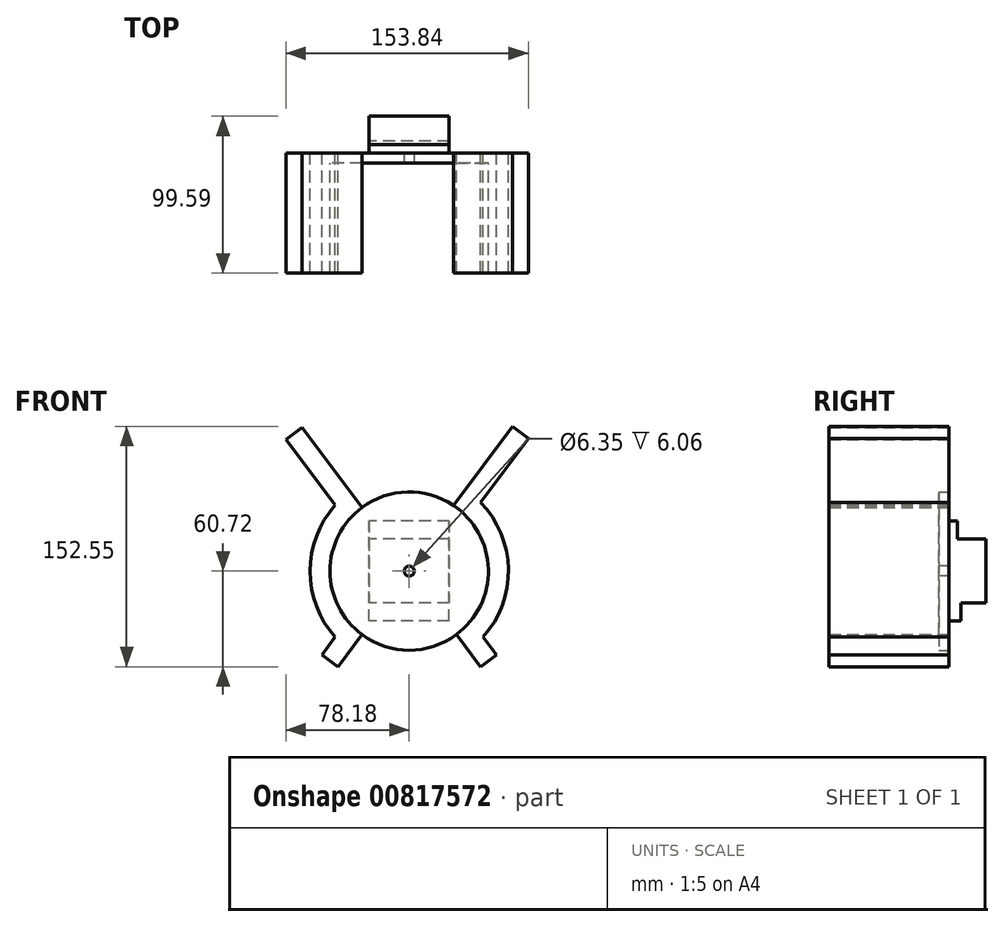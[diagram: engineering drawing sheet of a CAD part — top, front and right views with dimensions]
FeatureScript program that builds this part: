
annotation { "Feature Type Name" : "Feature", "Feature Type Description" : "" }
export const myFeature = defineFeature(function(context is Context, id is Id, definition is map)
    precondition{}
    {
        {
            var Q0;
            Q0=qCreatedBy(makeId("Front.planeOp"),FACE);
            var sketch = newSketch(context, id + "F0", { "sketchPlane" : qUnion([Q0])});
            skCircle(sketch, "E0", {"center": v(0, 0) * mm, "radius": 50.3 * mm});
            skLineSegment(sketch, "E1", {"start": v(-29.97, 40.39) * mm, "end": v(-68, 91.23) * mm});
            skLineSegment(sketch, "E2", {"start": v(-29.97, -40.39) * mm, "end": v(-45.19, -60.72) * mm});
            skLineSegment(sketch, "E3", {"start": v(29.97, -40.39) * mm, "end": v(45.19, -60.72) * mm});
            skLineSegment(sketch, "E4", {"start": v(65.5, 91.83) * mm, "end": v(75.66, 84.22) * mm});
            skLineSegment(sketch, "E5", {"start": v(75.66, 84.22) * mm, "end": v(37.62, 33.37) * mm});
            skLineSegment(sketch, "E6", {"start": v(-68, 91.23) * mm, "end": v(-78.18, 83.63) * mm});
            skLineSegment(sketch, "E7", {"start": v(-78.18, 83.63) * mm, "end": v(-39.2, 31.51) * mm});
            skLineSegment(sketch, "E8", {"start": v(-45.19, -60.72) * mm, "end": v(-55.36, -53.12) * mm});
            skLineSegment(sketch, "E9", {"start": v(-55.36, -53.12) * mm, "end": v(-39.2, -31.51) * mm});
            skLineSegment(sketch, "E10", {"start": v(45.19, -60.72) * mm, "end": v(55.36, -53.12) * mm});
            skLineSegment(sketch, "E11", {"start": v(55.36, -53.12) * mm, "end": v(39.2, -31.51) * mm});
            skLineSegment(sketch, "E12", {"start": v(65.5, 91.83) * mm, "end": v(28.03, 41.75) * mm});
            skCircle(sketch, "E13.0", {"center": v(0, 0) * mm, "radius": 63 * mm});
            skSolve(sketch);
        }
        {
            var Q0;
            {var subQ0=sQuery(id+"F0.wireOp",EDGE,"E1");Q0=makeQuery(id+"F0.imprint","IMPRINT",FACE,{"disambiguationData":[TD([[makeQuery(id+"F0.imprint","IMPRINT",EDGE,{"derivedFrom":subQ0}),1.0]])]});}
            var Q1;
            {var subQ4=sQuery(id+"F0.wireOp",EDGE,"E4");Q1=makeQuery(id+"F0.imprint","IMPRINT",FACE,{"disambiguationData":[TD([[makeQuery(id+"F0.imprint","IMPRINT",EDGE,{"derivedFrom":subQ4}),-1.0]])]});}
            var Q2;
            {var subQ0=sQuery(id+"F0.wireOp",EDGE,"E3");Q2=makeQuery(id+"F0.imprint","IMPRINT",FACE,{"disambiguationData":[TD([[makeQuery(id+"F0.imprint","IMPRINT",EDGE,{"derivedFrom":subQ0}),1.0]])]});}
            var Q3;
            {var subQ0=sQuery(id+"F0.wireOp",EDGE,"E2");Q3=makeQuery(id+"F0.imprint","IMPRINT",FACE,{"disambiguationData":[TD([[makeQuery(id+"F0.imprint","IMPRINT",EDGE,{"derivedFrom":subQ0}),-1.0]])]});}
            var Q4;
            {var subQ0=sQuery(id+"F0.wireOp",EDGE,"E5");var subQ1=sQuery(id+"F0.wireOp",EDGE,"E0");var subQ2=makeQuery(id+"F0.imprint","INTERSECT",VERTEX,{"derivedFrom":[subQ1,subQ0]});Q4=makeQuery(id+"F0.imprint","IMPRINT",FACE,{"disambiguationData":[TD([[makeQuery(id+"F0.imprint","IMPRINT",EDGE,{"disambiguationData":[TD([[subQ2,-1.0]])],"derivedFrom":subQ1}),-1.0]])]});}
            var Q5;
            {var subQ0=sQuery(id+"F0.wireOp",EDGE,"E7");var subQ1=sQuery(id+"F0.wireOp",EDGE,"E0");var subQ2=makeQuery(id+"F0.imprint","INTERSECT",VERTEX,{"derivedFrom":[subQ1,subQ0]});Q5=makeQuery(id+"F0.imprint","IMPRINT",FACE,{"disambiguationData":[TD([[makeQuery(id+"F0.imprint","IMPRINT",EDGE,{"disambiguationData":[TD([[subQ2,-1.0]])],"derivedFrom":subQ1}),-1.0]])]});}
            var Q6;
            {var subQ0=sQuery(id+"F0.wireOp",EDGE,"E5");var subQ1=sQuery(id+"F0.wireOp",EDGE,"E0");var subQ2=makeQuery(id+"F0.imprint","INTERSECT",VERTEX,{"derivedFrom":[subQ1,subQ0]});Q6=makeQuery(id+"F0.imprint","IMPRINT",FACE,{"disambiguationData":[TD([[makeQuery(id+"F0.imprint","IMPRINT",EDGE,{"disambiguationData":[TD([[subQ2,1.0]])],"derivedFrom":subQ1}),-1.0]])]});}
            var Q7;
            {var subQ0=sQuery(id+"F0.wireOp",EDGE,"E0");var subQ5=makeQuery(id+"F0.imprint","INTERSECT",VERTEX,{"derivedFrom":[subQ0,sQuery(id+"F0.wireOp",EDGE,"E5")]});Q7=makeQuery(id+"F0.imprint","IMPRINT",FACE,{"disambiguationData":[TD([[makeQuery(id+"F0.imprint","IMPRINT",EDGE,{"disambiguationData":[TD([[subQ5,-1.0]])],"derivedFrom":subQ0}),1.0]])]});}
            extrude(context, id + "F1", {"entities" : qUnion([Q0, Q1, Q2, Q3, Q4, Q5, Q6, Q7]), "endBound" : BoundingType.SYMMETRIC, "depth" : 76.2 * mm, "offsetDistance" : 25.4 * mm});
        }
        {
            var Q0;
            Q0=qCreatedBy(makeId("Front.planeOp"),FACE);
            var sketch = newSketch(context, id + "F2", { "sketchPlane" : qUnion([Q0])});
            skCircle(sketch, "E14", {"center": v(0, 0) * mm, "radius": 50.3 * mm});
            skSolve(sketch);
        }
        {
            var Q0;
            Q0 = qSketchRegion(id + "F2", true);
            var Q1;
            Q1=makeQuery(id+"F1.opExtrude","CAP_FACE",FACE,{"disambiguationData":[OSD([sQuery(id+"F0.wireOp",EDGE,"E0"),sQuery(id+"F0.wireOp",EDGE,"E1"),sQuery(id+"F0.wireOp",EDGE,"E2"),sQuery(id+"F0.wireOp",EDGE,"E3"),sQuery(id+"F0.wireOp",EDGE,"E4"),sQuery(id+"F0.wireOp",EDGE,"E5"),sQuery(id+"F0.wireOp",EDGE,"E6"),sQuery(id+"F0.wireOp",EDGE,"E7"),sQuery(id+"F0.wireOp",EDGE,"E8"),sQuery(id+"F0.wireOp",EDGE,"E9"),sQuery(id+"F0.wireOp",EDGE,"E10"),sQuery(id+"F0.wireOp",EDGE,"E11"),sQuery(id+"F0.wireOp",EDGE,"E12"),sQuery(id+"F0.wireOp",EDGE,"E13.0")])],"isStart":false});
            extrude(context, id + "F3", {"entities" : qUnion([Q0]), "operationType" : NewBodyOperationType.REMOVE, "endBound" : BoundingType.UP_TO_SURFACE, "depth" : 63.5 * mm, "endBoundEntityFace" : qUnion([Q1]), "offsetDistance" : 25.4 * mm, "hasSecondDirection" : true, "secondDirectionOppositeDirection" : true, "secondDirectionDepth" : 31.75 * mm});
        }
        {
            var Q0;
            Q0=qCreatedBy(makeId("Front.planeOp"),FACE);
            var sketch = newSketch(context, id + "F4", { "sketchPlane" : qUnion([Q0])});
            skCircle(sketch, "E15", {"center": v(0, 0) * mm, "radius": 3.18 * mm});
            skSolve(sketch);
        }
        {
            var Q0;
            Q0=makeQuery(id+"F4.imprint","IMPRINT",FACE,{"disambiguationData":[TD([[makeQuery(id+"F4.imprint","IMPRINT",EDGE,{"derivedFrom":sQuery(id+"F4.wireOp",EDGE,"E15")}),1.0]])]});
            extrude(context, id + "F5", {"entities" : qUnion([Q0]), "operationType" : NewBodyOperationType.REMOVE, "endBound" : BoundingType.THROUGH_ALL, "oppositeDirection" : true, "depth" : 25.4 * mm, "offsetDistance" : 25.4 * mm});
        }
        {
            var Q0;
            Q0=qCreatedBy(makeId("Right.planeOp"),FACE);
            var sketch = newSketch(context, id + "F6", { "sketchPlane" : qUnion([Q0])});
            skLineSegment(sketch, "E16.bottom", {"start": v(37.8, 20.38) * mm, "end": v(61.5, 20.38) * mm});
            skLineSegment(sketch, "E16.top", {"start": v(37.8, -20.38) * mm, "end": v(61.5, -20.38) * mm});
            skLineSegment(sketch, "E16.left", {"start": v(37.8, 20.38) * mm, "end": v(37.8, -20.38) * mm});
            skLineSegment(sketch, "E16.right", {"start": v(61.5, 20.38) * mm, "end": v(61.5, -20.38) * mm});
            skPoint(sketch, "E16.middle", {"position": v(49.65, 0) * mm});
            skLineSegment(sketch, "E17", {"start": v(37.9, 31.93) * mm, "end": v(37.8, 20.38) * mm});
            skLineSegment(sketch, "E18", {"start": v(37.9, 31.93) * mm, "end": v(43.55, 31.88) * mm});
            skLineSegment(sketch, "E19", {"start": v(43.55, 31.88) * mm, "end": v(43.45, 20.38) * mm});
            skLineSegment(sketch, "E20", {"start": v(37.8, -20.38) * mm, "end": v(37.8, -31.8) * mm});
            skLineSegment(sketch, "E21", {"start": v(37.8, -31.8) * mm, "end": v(45.76, -31.8) * mm});
            skLineSegment(sketch, "E22", {"start": v(45.76, -31.8) * mm, "end": v(45.76, -20.38) * mm});
            skSolve(sketch);
        }
        {
            var Q0;
            Q0 = qSketchRegion(id + "F6", true);
            extrude(context, id + "F7", {"entities" : qUnion([Q0]), "operationType" : NewBodyOperationType.ADD, "endBound" : BoundingType.SYMMETRIC, "depth" : 50.8 * mm, "offsetDistance" : 25.4 * mm});
        }
    });
